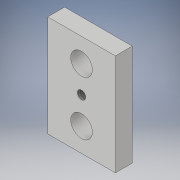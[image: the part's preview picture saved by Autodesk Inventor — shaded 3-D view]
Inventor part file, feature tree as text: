
AUTODESK INVENTOR PART (.ipt)
format: ipt  version: 2017 (Build 210142000, 142)  size: 114,176 bytes
history: native  units: in
note: dims shown in document units (in); Inventor stores cm internally (conversion verified against a paired STEP export)
features: extrude x2, sketch x2, hole x2
ambient origin geometry x8: Origin, YZ Plane, XZ Plane, XY Plane, X Axis, Y Axis, Z Axis, Center Point
bodies: Solid1 (feature_tree)
feature tree (6):
  extrude  "Extrusion1"  Depth=0.75in
  sketch  "Sketch2"  dims[d2=0.125in d3=0.0in d4=0.175in d5=0.16in d6=0.062in d7=0.157in d8=0.375in d9=0.25in d10=0.5635in d11=0.248in d12=0.8108in d13=1.0in d14=0.0in d15=0.175in d16=0.16in d17=0.157in d18=0.375in d19=0.25in d20=0.5635in d21=0.248in d22=0.8108in]
  hole  "Hole1"  [1 undecoded]
  extrude  "Extrusion2"  Depth=0.125in
  hole  "Hole2"  [1 undecoded]
  sketch  "Sketch1"  dims[d0=0.5in d1=0.75in]
note: 2 required parameter values undecoded (feature->parameter linkage not recoverable at this tier; creation-order binding heuristic only, values carry confidence <= 0.55)
